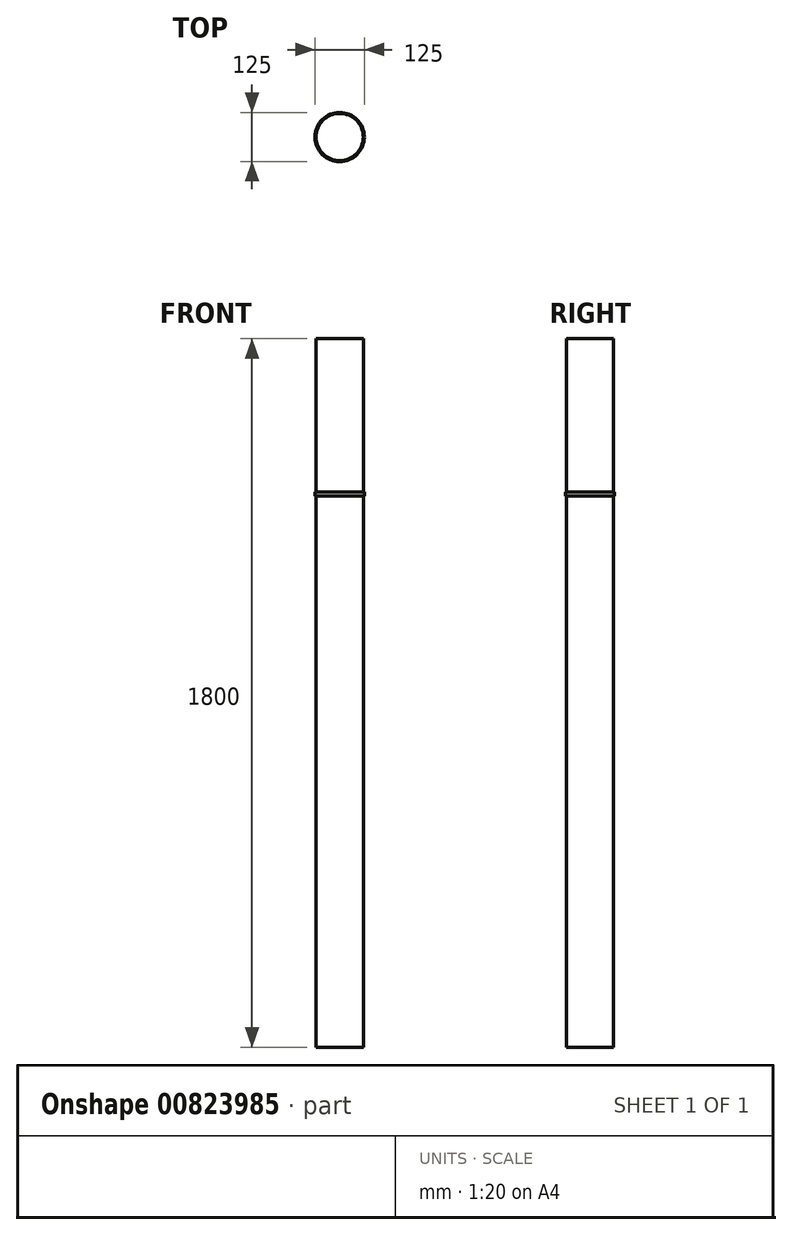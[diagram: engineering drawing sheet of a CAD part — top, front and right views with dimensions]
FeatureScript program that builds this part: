
annotation { "Feature Type Name" : "Feature", "Feature Type Description" : "" }
export const myFeature = defineFeature(function(context is Context, id is Id, definition is map)
    precondition{}
    {
        {
            var Q0;
            Q0=qCreatedBy(makeId("Top.planeOp"),FACE);
            var sketch = newSketch(context, id + "F0", { "sketchPlane" : qUnion([Q0])});
            skCircle(sketch, "E0", {"center": v(0, 0) * mm, "radius": 60 * mm});
            skSolve(sketch);
        }
        {
            var Q0;
            Q0=makeQuery(id+"F0.imprint","IMPRINT",FACE,{"disambiguationData":[TD([[makeQuery(id+"F0.imprint","IMPRINT",EDGE,{"derivedFrom":sQuery(id+"F0.wireOp",EDGE,"E0")}),1.0]])]});
            extrude(context, id + "F1", {"entities" : qUnion([Q0]), "depth" : 900 * mm, "offsetDistance" : 25 * mm});
        }
        {
            var Q0;
            Q0=makeQuery(id+"F1.opExtrude","SWEPT_BODY",BODY,{"disambiguationData":[OSD([sQuery(id+"F0.wireOp",EDGE,"E0")])]});
            var Q1;
            Q1=qCreatedBy(makeId("Top.planeOp"),FACE);
            mirror(context, id + "F2", {"operationType" : NewBodyOperationType.ADD, "entities" : qUnion([Q0]), "mirrorPlane" : qUnion([Q1])});
        }
        {
            var Q0;
            Q0=qCreatedBy(makeId("Top.planeOp"),FACE);
            cPlane(context, id + "F3", {"entities" : qUnion([Q0]), "cplaneType" : CPlaneType.OFFSET, "offset" : 500 * mm, "width" : 150 * mm, "height" : 150 * mm});
        }
        {
            var Q0;
            Q0=qCreatedBy(id+"F3.planeOp",FACE);
            var sketch = newSketch(context, id + "F4", { "sketchPlane" : qUnion([Q0])});
            skCircle(sketch, "E1", {"center": v(0, 0) * mm, "radius": 62.5 * mm});
            skCircle(sketch, "E2.0", {"center": v(0, 0) * mm, "radius": 60 * mm});
            skSolve(sketch);
        }
        {
            var Q0;
            Q0 = qSketchRegion(id + "F4", true);
            extrude(context, id + "F5", {"entities" : qUnion([Q0]), "operationType" : NewBodyOperationType.ADD, "depth" : 10 * mm, "offsetDistance" : 25 * mm});
        }
    });
